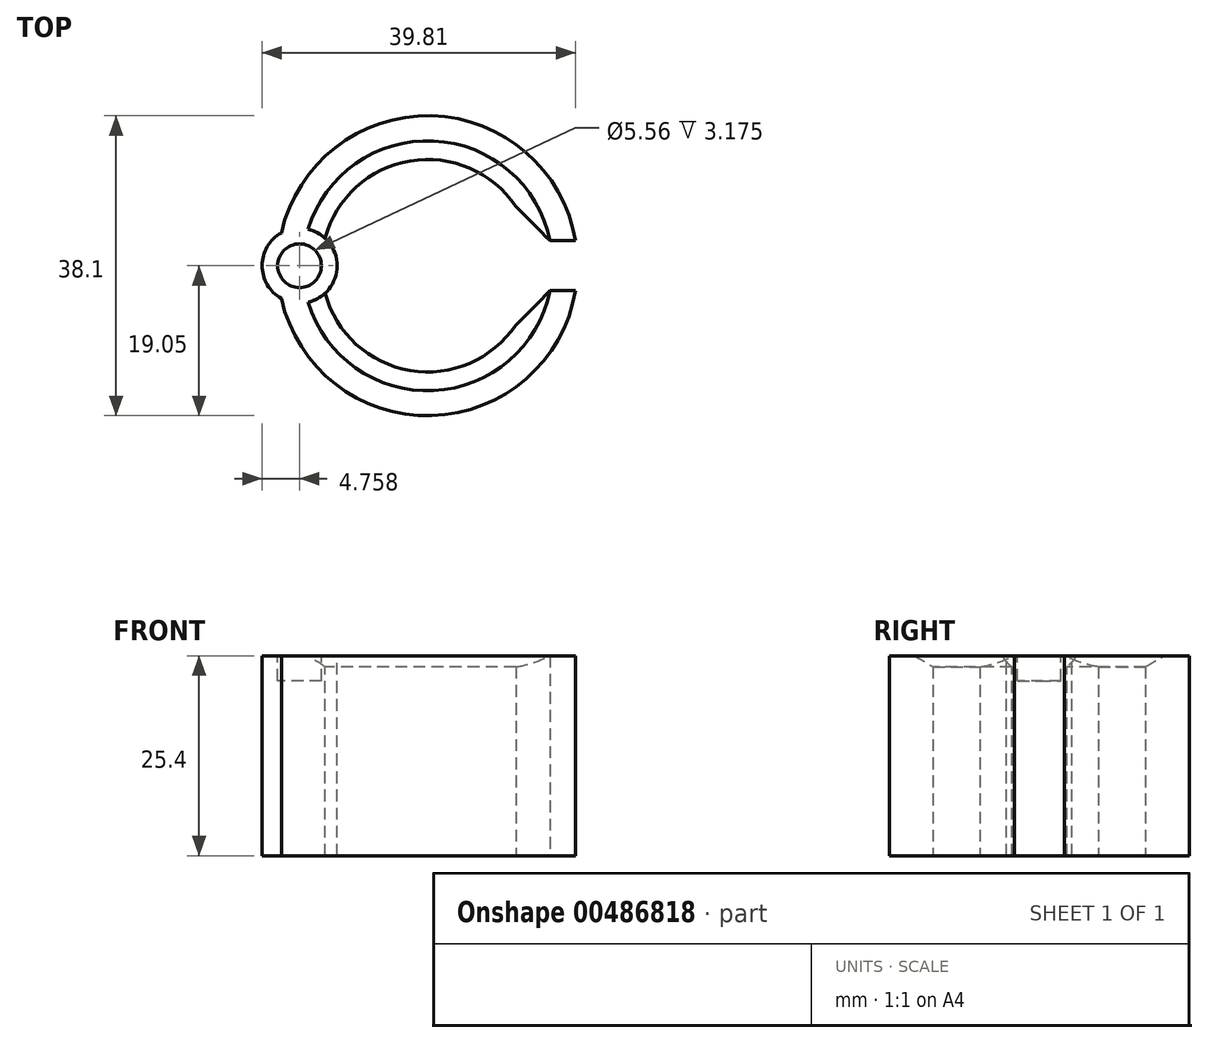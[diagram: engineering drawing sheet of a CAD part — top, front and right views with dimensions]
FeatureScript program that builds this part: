
annotation { "Feature Type Name" : "Feature", "Feature Type Description" : "" }
export const myFeature = defineFeature(function(context is Context, id is Id, definition is map)
    precondition{}
    {
        {
            var Q0;
            Q0=qCreatedBy(makeId("Top.planeOp"),FACE);
            var sketch = newSketch(context, id + "F0", { "sketchPlane" : qUnion([Q0])});
            skLineSegment(sketch, "E0.bottom", {"start": v(38.1, 19.05) * mm, "end": v(-38.1, 19.05) * mm, "construction": true});
            skLineSegment(sketch, "E0.top", {"start": v(38.1, -19.05) * mm, "end": v(-38.1, -19.05) * mm, "construction": true});
            skLineSegment(sketch, "E0.left", {"start": v(38.1, 19.05) * mm, "end": v(38.1, -19.05) * mm, "construction": true});
            skLineSegment(sketch, "E0.right", {"start": v(-38.1, 19.05) * mm, "end": v(-38.1, -19.05) * mm, "construction": true});
            skPoint(sketch, "E0.middle", {"position": v(0, 0) * mm});
            skArc(sketch, "E1", {"start": v(18.78, 3.18) * mm, "mid": v(-19.05, 0) * mm, "end": v(18.78, -3.18) * mm});
            skArc(sketch, "E2.0", {"start": v(15.55, 3.18) * mm, "mid": v(-15.88, 0) * mm, "end": v(15.55, -3.18) * mm});
            skLineSegment(sketch, "E3", {"start": v(-20.37, 0) * mm, "end": v(20.37, 0) * mm, "construction": true});
            skLineSegment(sketch, "E4.0", {"start": v(-20.37, 3.18) * mm, "end": v(20.37, 3.18) * mm, "construction": true});
            skLineSegment(sketch, "E5.0", {"start": v(-20.37, -3.18) * mm, "end": v(20.37, -3.18) * mm, "construction": true});
            skLineSegment(sketch, "E6", {"start": v(15.55, 3.18) * mm, "end": v(18.78, 3.18) * mm});
            skLineSegment(sketch, "E7", {"start": v(15.55, -3.18) * mm, "end": v(18.78, -3.18) * mm});
            skLineSegment(sketch, "E8", {"start": v(18.78, 3.18) * mm, "end": v(18.78, -3.18) * mm, "construction": true});
            skArc(sketch, "E9.0", {"start": v(11.2, 7.54) * mm, "mid": v(-13.5, 0) * mm, "end": v(11.2, -7.54) * mm});
            skLineSegment(sketch, "E10", {"start": v(11.2, 7.54) * mm, "end": v(11.2, -7.54) * mm, "construction": true});
            skLineSegment(sketch, "E11", {"start": v(15.55, 3.17) * mm, "end": v(11.2, 7.54) * mm});
            skLineSegment(sketch, "E12", {"start": v(15.55, -3.18) * mm, "end": v(11.2, -7.54) * mm});
            skCircle(sketch, "E13", {"center": v(0, 0) * mm, "radius": 16.27 * mm, "construction": true});
            skSolve(sketch);
        }
        {
            var Q0;
            Q0=makeQuery(id+"F0.imprint","IMPRINT",FACE,{"disambiguationData":[TD([[makeQuery(id+"F0.imprint","IMPRINT",EDGE,{"derivedFrom":sQuery(id+"F0.wireOp",EDGE,"E1")}),1.0]])]});
            var Q1;
            Q1=makeQuery(id+"F0.imprint","IMPRINT",FACE,{"disambiguationData":[TD([[makeQuery(id+"F0.imprint","IMPRINT",EDGE,{"derivedFrom":sQuery(id+"F0.wireOp",EDGE,"E2.0")}),1.0]])]});
            extrude(context, id + "F1", {"entities" : qUnion([Q0, Q1]), "depth" : 25.4 * mm});
        }
        {
            var Q0;
            Q0=makeQuery(id+"F1.opExtrude","SWEPT_FACE",FACE,{"disambiguationData":[OSD([sQuery(id+"F0.wireOp",EDGE,"E6")])]});
            var sketch = newSketch(context, id + "F2", { "sketchPlane" : qUnion([Q0])});
            skLineSegment(sketch, "E14", {"start": v(15.55, 25.4) * mm, "end": v(12.38, 23.57) * mm});
            skLineSegment(sketch, "E15", {"start": v(12.38, 23.57) * mm, "end": v(15.55, 23.57) * mm, "construction": true});
            skLineSegment(sketch, "E16", {"start": v(15.55, 23.57) * mm, "end": v(15.55, 25.4) * mm, "construction": true});
            skLineSegment(sketch, "E17", {"start": v(12.38, 23.57) * mm, "end": v(12.38, 25.4) * mm});
            skLineSegment(sketch, "E18", {"start": v(12.38, 25.4) * mm, "end": v(15.55, 25.4) * mm});
            skSolve(sketch);
        }
        {
            var Q0;
            Q0 = qSketchRegion(id + "F2", true);
            var Q1;
            Q1=makeQuery(id+"F1.opExtrude","SWEPT_FACE",FACE,{"disambiguationData":[OSD([sQuery(id+"F0.wireOp",EDGE,"E9.0")])]});
            revolve(context, id + "F3", {"operationType" : NewBodyOperationType.REMOVE, "entities" : qUnion([Q0]), "axis" : qUnion([Q1]), "revolveType" : RevolveType.FULL, "oppositeDirection" : true});
        }
        {
            var Q0;
            Q0=makeQuery(id+"F1.opExtrude","CAP_FACE",FACE,{"disambiguationData":[OSD([sQuery(id+"F0.wireOp",EDGE,"E1"),sQuery(id+"F0.wireOp",EDGE,"E6"),sQuery(id+"F0.wireOp",EDGE,"E7"),sQuery(id+"F0.wireOp",EDGE,"E9.0"),sQuery(id+"F0.wireOp",EDGE,"E11"),sQuery(id+"F0.wireOp",EDGE,"E12")])],"isStart":false});
            var sketch = newSketch(context, id + "F4", { "sketchPlane" : qUnion([Q0])});
            skCircle(sketch, "E19", {"center": v(0, 0) * mm, "radius": 16.27 * mm, "construction": true});
            skCircle(sketch, "E20", {"center": v(-16.27, 0) * mm, "radius": 4.76 * mm});
            skSolve(sketch);
        }
        {
            var Q0;
            Q0 = qSketchRegion(id + "F4", true);
            extrude(context, id + "F5", {"entities" : qUnion([Q0]), "operationType" : NewBodyOperationType.ADD, "oppositeDirection" : true, "depth" : 25.4 * mm});
        }
        {
            var Q0;
            Q0=makeQuery(id+"F5.boolean.opBoolean","MERGE",FACE,{"derivedFrom":[makeQuery(id+"F1.opExtrude","CAP_FACE",FACE,{"disambiguationData":[OSD([sQuery(id+"F0.wireOp",EDGE,"E1"),sQuery(id+"F0.wireOp",EDGE,"E6"),sQuery(id+"F0.wireOp",EDGE,"E7"),sQuery(id+"F0.wireOp",EDGE,"E9.0"),sQuery(id+"F0.wireOp",EDGE,"E11"),sQuery(id+"F0.wireOp",EDGE,"E12")])],"isStart":false}),makeQuery(id+"F5.opExtrude","CAP_FACE",FACE,{"disambiguationData":[OSD([sQuery(id+"F4.wireOp",EDGE,"E20")])],"isStart":true})]});
            var sketch = newSketch(context, id + "F6", { "sketchPlane" : qUnion([Q0])});
            skCircle(sketch, "E21", {"center": v(-16.27, 0) * mm, "radius": 2.78 * mm});
            skSolve(sketch);
        }
        {
            var Q0;
            Q0=makeQuery(id+"F6.imprint","IMPRINT",FACE,{"disambiguationData":[TD([[makeQuery(id+"F6.imprint","IMPRINT",EDGE,{"derivedFrom":sQuery(id+"F6.wireOp",EDGE,"E21")}),1.0]])]});
            extrude(context, id + "F7", {"entities" : qUnion([Q0]), "operationType" : NewBodyOperationType.REMOVE, "oppositeDirection" : true, "depth" : 3.17 * mm});
        }
        {
            var Q0;
            Q0=makeQuery(id+"F5.boolean.opBoolean","MERGE",FACE,{"derivedFrom":[makeQuery(id+"F1.opExtrude","CAP_FACE",FACE,{"disambiguationData":[OSD([sQuery(id+"F0.wireOp",EDGE,"E1"),sQuery(id+"F0.wireOp",EDGE,"E6"),sQuery(id+"F0.wireOp",EDGE,"E7"),sQuery(id+"F0.wireOp",EDGE,"E9.0"),sQuery(id+"F0.wireOp",EDGE,"E11"),sQuery(id+"F0.wireOp",EDGE,"E12")])],"isStart":false}),makeQuery(id+"F5.opExtrude","CAP_FACE",FACE,{"disambiguationData":[OSD([sQuery(id+"F4.wireOp",EDGE,"E20")])],"isStart":true})]});
            cPlane(context, id + "F8", {"entities" : qUnion([Q0]), "cplaneType" : CPlaneType.OFFSET, "offset" : 0.8 * mm, "oppositeDirection" : true, "width" : 152.4 * mm, "height" : 152.4 * mm});
        }
    });
